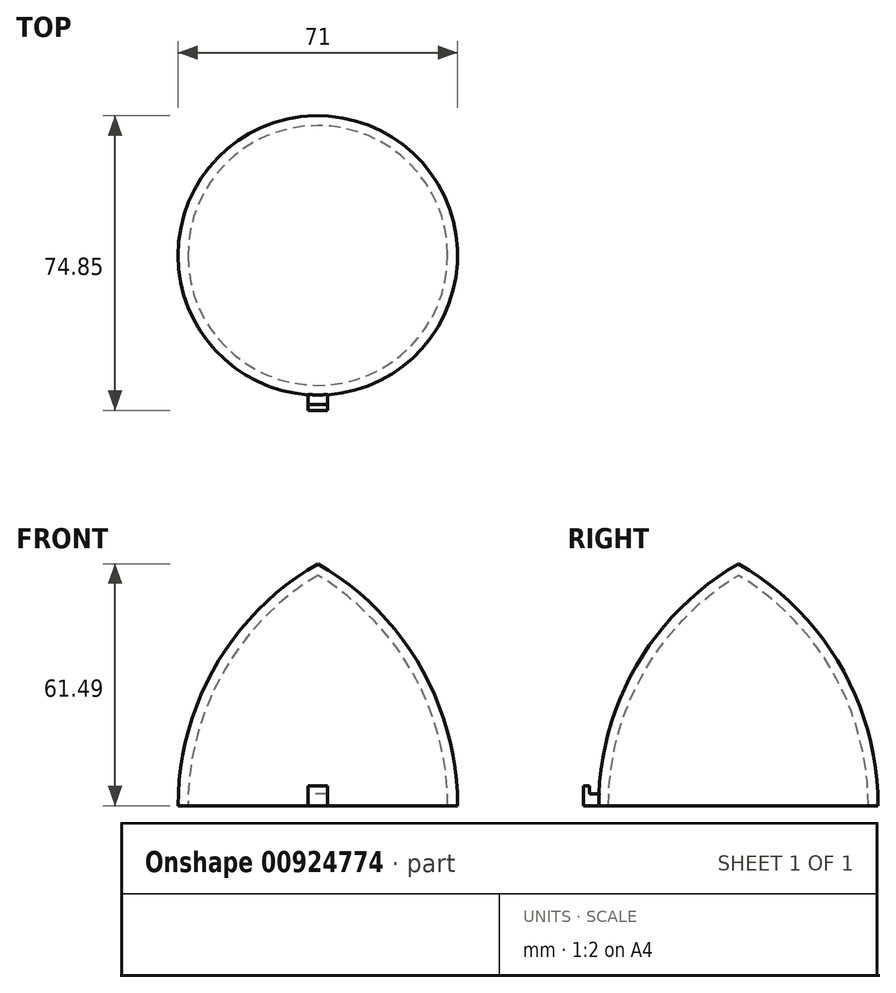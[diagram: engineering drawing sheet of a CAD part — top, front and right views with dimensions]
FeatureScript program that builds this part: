
annotation { "Feature Type Name" : "Feature", "Feature Type Description" : "" }
export const myFeature = defineFeature(function(context is Context, id is Id, definition is map)
    precondition{}
    {
        {
            var Q0;
            Q0=qCreatedBy(makeId("Front.planeOp"),FACE);
            var sketch = newSketch(context, id + "F0", { "sketchPlane" : qUnion([Q0])});
            skArc(sketch, "E0.cCircle", {"start": v(0, 20.5) * mm, "mid": v(-20.5, 0) * mm, "end": v(0, -20.5) * mm, "construction": true});
            skLineSegment(sketch, "E0.1", {"start": v(0, -20.5) * mm, "end": v(-35.5, -20.5) * mm});
            skLineSegment(sketch, "E0.2", {"start": v(-35.5, -20.5) * mm, "end": v(0, 41) * mm});
            skPoint(sketch, "E0.0.midPoint", {"position": v(17.75, 10.25) * mm});
            skArc(sketch, "E1", {"start": v(0, 41) * mm, "mid": v(-25.99, 15) * mm, "end": v(-35.5, -20.5) * mm});
            skLineSegment(sketch, "E2", {"start": v(0, 41) * mm, "end": v(0, -20.5) * mm});
            skArc(sketch, "E3.0", {"start": v(0, 38.09) * mm, "mid": v(-24.18, 13.12) * mm, "end": v(-33, -20.5) * mm});
            skSolve(sketch);
        }
        {
            var Q0;
            {var subQ0=sQuery(id+"F0.wireOp",EDGE,"E1");Q0=makeQuery(id+"F0.imprint","IMPRINT",FACE,{"disambiguationData":[TD([[makeQuery(id+"F0.imprint","IMPRINT",EDGE,{"derivedFrom":subQ0}),1.0]])]});}
            var Q1;
            {var subQ1=sQuery(id+"F0.wireOp",EDGE,"E0.1");var subQ3=sQuery(id+"F0.wireOp",EDGE,"E3.0");var subQ4=makeQuery(id+"F0.imprint","INTERSECT",VERTEX,{"derivedFrom":[subQ1,subQ3]});Q1=makeQuery(id+"F0.imprint","IMPRINT",FACE,{"disambiguationData":[TD([[makeQuery(id+"F0.imprint","IMPRINT",EDGE,{"disambiguationData":[TD([[subQ4,1.0]])],"derivedFrom":subQ3}),-1.0]])]});}
            var Q2;
            {var subQ0=sQuery(id+"F0.wireOp",EDGE,"E2");var subQ3=sQuery(id+"F0.wireOp",EDGE,"E3.0");var subQ5=makeQuery(id+"F0.imprint","INTERSECT",VERTEX,{"derivedFrom":[subQ0,subQ3]});Q2=makeQuery(id+"F0.imprint","IMPRINT",FACE,{"disambiguationData":[TD([[makeQuery(id+"F0.imprint","IMPRINT",EDGE,{"disambiguationData":[TD([[subQ5,-1.0]])],"derivedFrom":subQ3}),-1.0]])]});}
            var Q3;
            Q3=sQuery(id+"F0.wireOp",EDGE,"E2");
            revolve(context, id + "F1", {"surfaceOperationType" : NewSurfaceOperationType.NEW, "entities" : qUnion([Q0, Q1, Q2]), "axis" : qUnion([Q3]), "revolveType" : RevolveType.FULL});
        }
        {
            var Q0;
            Q0=makeQuery(id+"F1.opRevolve","SWEPT_FACE",FACE,{"disambiguationData":[OSD([sQuery(id+"F0.wireOp",EDGE,"E0.1")])]});
            var sketch = newSketch(context, id + "F2", { "sketchPlane" : qUnion([Q0])});
            skLineSegment(sketch, "E4.bottom", {"start": v(2.44, 39.35) * mm, "end": v(-2.44, 39.35) * mm});
            skLineSegment(sketch, "E4.left", {"start": v(2.44, 39.35) * mm, "end": v(2.44, 34.35) * mm});
            skLineSegment(sketch, "E4.right", {"start": v(-2.44, 39.35) * mm, "end": v(-2.44, 34.35) * mm});
            skPoint(sketch, "E4.middle", {"position": v(0, 0) * mm});
            skArc(sketch, "E5", {"start": v(2.44, 34.35) * mm, "mid": v(0, 34.43) * mm, "end": v(-2.44, 34.35) * mm});
            skLineSegment(sketch, "E6", {"start": v(0, 0) * mm, "end": v(0, 34.43) * mm});
            skSolve(sketch);
        }
        {
            var Q0;
            {var subQ0=sQuery(id+"F2.wireOp",EDGE,"E4.bottom");Q0=makeQuery(id+"F2.imprint","IMPRINT",FACE,{"disambiguationData":[TD([[makeQuery(id+"F2.imprint","IMPRINT",EDGE,{"derivedFrom":subQ0}),1.0]])]});}
            var Q1;
            {var subQ0=sQuery(id+"F2.wireOp",EDGE,"E5");Q1=makeQuery(id+"F2.imprint","IMPRINT",FACE,{"disambiguationData":[TD([[makeQuery(id+"F2.imprint","IMPRINT",EDGE,{"derivedFrom":subQ0}),-1.0]])]});}
            extrude(context, id + "F3", {"entities" : qUnion([Q0, Q1]), "operationType" : NewBodyOperationType.ADD, "oppositeDirection" : true, "depth" : 3 * mm, "offsetDistance" : 25 * mm});
        }
        {
            var Q0;
            Q0=makeQuery(id+"F3.opExtrude","CAP_FACE",FACE,{"disambiguationData":[OSD([sQuery(id+"F2.wireOp",EDGE,"E4.bottom"),sQuery(id+"F2.wireOp",EDGE,"E4.left"),sQuery(id+"F2.wireOp",EDGE,"E4.right"),sQuery(id+"F2.wireOp",EDGE,"E5")])],"isStart":false});
            var sketch = newSketch(context, id + "F4", { "sketchPlane" : qUnion([Q0])});
            skLineSegment(sketch, "E7.bottom", {"start": v(2.44, -39.35) * mm, "end": v(-2.44, -39.35) * mm});
            skLineSegment(sketch, "E7.top", {"start": v(2.44, -37.85) * mm, "end": v(-2.44, -37.85) * mm});
            skLineSegment(sketch, "E7.left", {"start": v(2.44, -39.35) * mm, "end": v(2.44, -37.85) * mm});
            skLineSegment(sketch, "E7.right", {"start": v(-2.44, -39.35) * mm, "end": v(-2.44, -37.85) * mm});
            skSolve(sketch);
        }
        {
            var Q0;
            Q0=makeQuery(id+"F4.imprint","IMPRINT",FACE,{"disambiguationData":[TD([[makeQuery(id+"F4.imprint","IMPRINT",EDGE,{"derivedFrom":sQuery(id+"F4.wireOp",EDGE,"E7.bottom")}),-1.0]])]});
            extrude(context, id + "F5", {"entities" : qUnion([Q0]), "operationType" : NewBodyOperationType.ADD, "depth" : 2 * mm, "offsetDistance" : 25 * mm});
        }
    });
